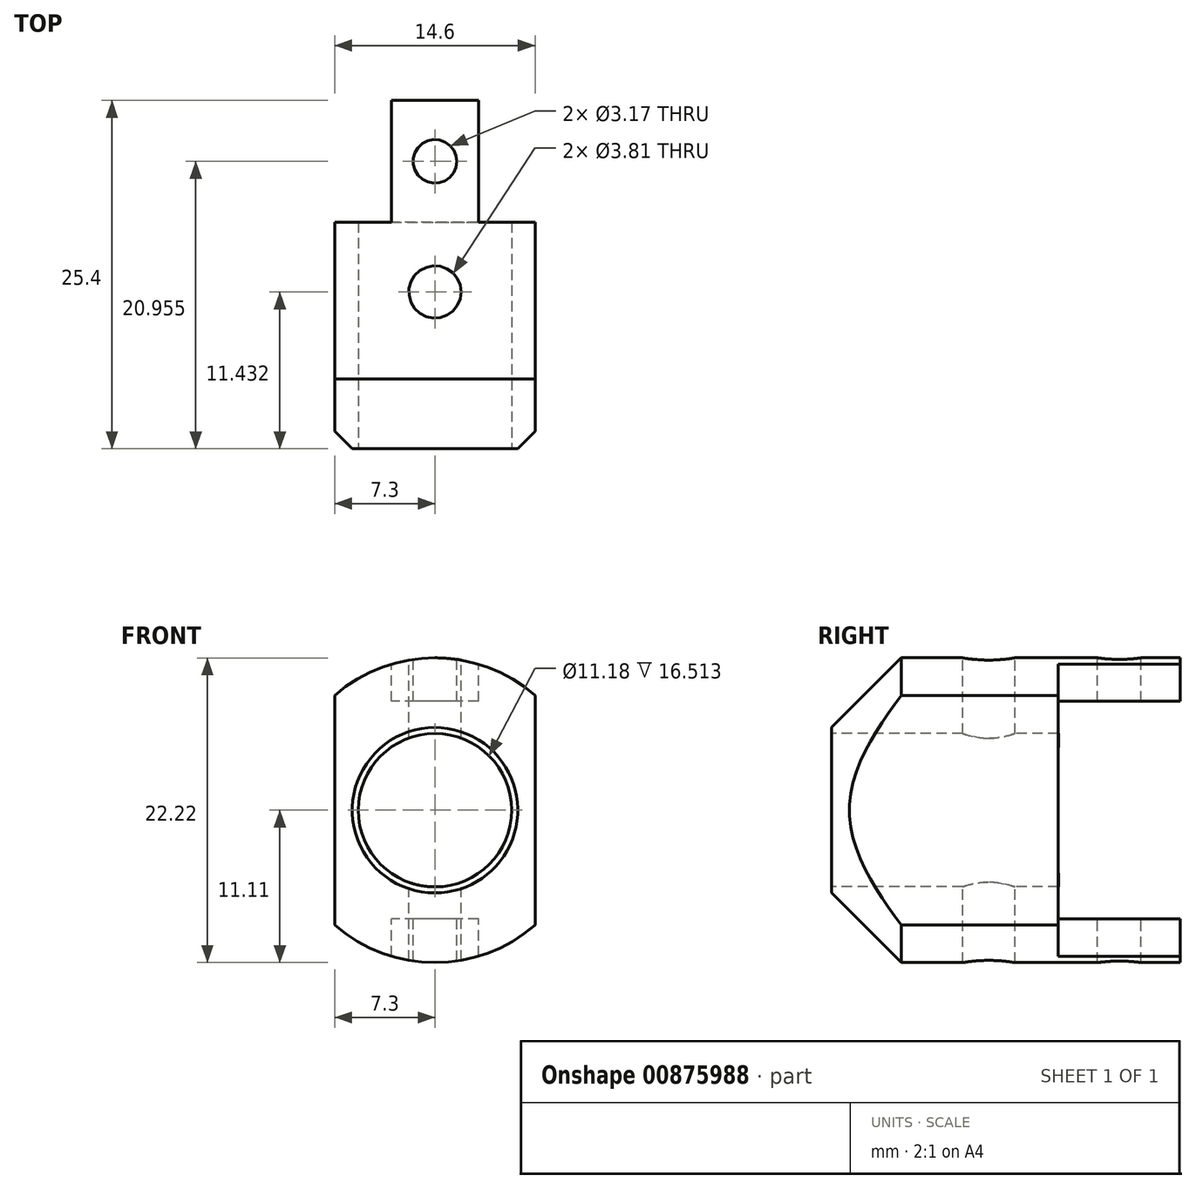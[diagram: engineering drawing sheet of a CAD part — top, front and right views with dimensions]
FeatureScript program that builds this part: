
annotation { "Feature Type Name" : "Feature", "Feature Type Description" : "" }
export const myFeature = defineFeature(function(context is Context, id is Id, definition is map)
    precondition{}
    {
        {
            var Q0;
            Q0=qCreatedBy(makeId("Front.planeOp"),FACE);
            var sketch = newSketch(context, id + "F0", { "sketchPlane" : qUnion([Q0])});
            skCircle(sketch, "E0", {"center": v(0, 0) * mm, "radius": 11.11 * mm});
            skSolve(sketch);
        }
        {
            var Q0;
            Q0=makeQuery(id+"F0.imprint","IMPRINT",FACE,{"disambiguationData":[TD([[makeQuery(id+"F0.imprint","IMPRINT",EDGE,{"derivedFrom":sQuery(id+"F0.wireOp",EDGE,"E0")}),1.0]])]});
            extrude(context, id + "F1", {"entities" : qUnion([Q0]), "endBound" : BoundingType.SYMMETRIC, "depth" : 25.4 * mm, "offsetDistance" : 25.4 * mm});
        }
        {
            var Q0;
            Q0=makeQuery(id+"F1.opExtrude","CAP_FACE",FACE,{"disambiguationData":[OSD([sQuery(id+"F0.wireOp",EDGE,"E0")])],"isStart":false});
            var sketch = newSketch(context, id + "F2", { "sketchPlane" : qUnion([Q0])});
            skCircle(sketch, "E1", {"center": v(0, 0) * mm, "radius": 5.59 * mm});
            skSolve(sketch);
        }
        {
            var Q0;
            Q0=makeQuery(id+"F2.imprint","IMPRINT",FACE,{"disambiguationData":[TD([[makeQuery(id+"F2.imprint","IMPRINT",EDGE,{"derivedFrom":sQuery(id+"F2.wireOp",EDGE,"E1")}),1.0]])]});
            extrude(context, id + "F3", {"entities" : qUnion([Q0]), "operationType" : NewBodyOperationType.REMOVE, "oppositeDirection" : true, "depth" : 31.75 * mm, "offsetDistance" : 25.4 * mm});
        }
        {
            var Q0;
            Q0=makeQuery(id+"F1.opExtrude","CAP_EDGE",EDGE,{"disambiguationData":[OSD([sQuery(id+"F0.wireOp",EDGE,"E0")])],"isStart":false});
            chamfer(context, id + "F4", {"entities" : qUnion([Q0]), "width" : 5.08 * mm, "tangentPropagation" : true});
        }
        {
            var Q0;
            Q0=makeQuery(id+"F1.opExtrude","CAP_FACE",FACE,{"disambiguationData":[OSD([sQuery(id+"F0.wireOp",EDGE,"E0")])],"isStart":true});
            var sketch = newSketch(context, id + "F5", { "sketchPlane" : qUnion([Q0])});
            skLineSegment(sketch, "E2.0", {"start": v(-7.3, 8.38) * mm, "end": v(-7.3, -8.38) * mm});
            skLineSegment(sketch, "E3.MirrorCS", {"start": v(7.3, 8.38) * mm, "end": v(7.3, -8.38) * mm});
            skArc(sketch, "E4", {"start": v(-7.3, 8.38) * mm, "mid": v(-11.11, 0) * mm, "end": v(-7.3, -8.38) * mm});
            skPoint(sketch, "E5.orphan", {"position": v(7.3, 14.3) * mm});
            skPoint(sketch, "E6.orphan", {"position": v(7.3, -21.1) * mm});
            skArc(sketch, "E7.trimOffspring", {"start": v(7.3, -8.38) * mm, "mid": v(11.11, 0) * mm, "end": v(7.3, 8.38) * mm});
            skPoint(sketch, "E8.orphan", {"position": v(-7.3, -21.1) * mm});
            skPoint(sketch, "E9.orphan", {"position": v(-7.3, 14.3) * mm});
            skPoint(sketch, "E10.orphan", {"position": v(0, 14.3) * mm});
            skSolve(sketch);
        }
        {
            var Q0;
            Q0=makeQuery(id+"F5.imprint","IMPRINT",FACE,{"disambiguationData":[TD([[makeQuery(id+"F5.imprint","IMPRINT",EDGE,{"derivedFrom":sQuery(id+"F5.wireOp",EDGE,"E3.MirrorCS")}),1.0]])]});
            var Q1;
            Q1=makeQuery(id+"F5.imprint","IMPRINT",FACE,{"disambiguationData":[TD([[makeQuery(id+"F5.imprint","IMPRINT",EDGE,{"derivedFrom":sQuery(id+"F5.wireOp",EDGE,"E2.0")}),-1.0]])]});
            extrude(context, id + "F6", {"entities" : qUnion([Q0, Q1]), "operationType" : NewBodyOperationType.REMOVE, "oppositeDirection" : true, "depth" : 31.75 * mm, "offsetDistance" : 25.4 * mm});
        }
        {
            var Q0;
            Q0=qCreatedBy(makeId("Top.planeOp"),FACE);
            cPlane(context, id + "F7", {"entities" : qUnion([Q0]), "cplaneType" : CPlaneType.OFFSET, "offset" : 11.1 * mm, "width" : 152.4 * mm, "height" : 152.4 * mm});
        }
        {
            var Q0;
            Q0=qCreatedBy(id+"F7.planeOp",FACE);
            var sketch = newSketch(context, id + "F8", { "sketchPlane" : qUnion([Q0])});
            skLineSegment(sketch, "E11", {"start": v(0, -12.7) * mm, "end": v(0, -1.27) * mm});
            skCircle(sketch, "E12", {"center": v(0, -1.27) * mm, "radius": 1.9 * mm});
            skLineSegment(sketch, "E13", {"start": v(0, 12.7) * mm, "end": v(0, 3.81) * mm});
            skLineSegment(sketch, "E14.0", {"start": v(-3.18, 12.7) * mm, "end": v(-3.18, 3.81) * mm});
            skLineSegment(sketch, "E15", {"start": v(-3.18, 3.81) * mm, "end": v(-7.3, 3.81) * mm});
            skLineSegment(sketch, "E16", {"start": v(-3.18, 12.7) * mm, "end": v(-7.3, 12.7) * mm});
            skLineSegment(sketch, "E17.0", {"start": v(-7.3, 12.7) * mm, "end": v(-7.3, 3.81) * mm});
            skLineSegment(sketch, "E18.MirrorCS", {"start": v(3.18, 12.7) * mm, "end": v(3.18, 3.81) * mm});
            skLineSegment(sketch, "E19.MirrorCS", {"start": v(3.18, 12.7) * mm, "end": v(7.3, 12.7) * mm});
            skLineSegment(sketch, "E20.MirrorCS", {"start": v(7.3, 12.7) * mm, "end": v(7.3, 3.81) * mm});
            skLineSegment(sketch, "E21.MirrorCS", {"start": v(3.18, 3.81) * mm, "end": v(7.3, 3.81) * mm});
            skCircle(sketch, "E22", {"center": v(0, 8.26) * mm, "radius": 1.59 * mm});
            skSolve(sketch);
        }
        {
            var Q0;
            Q0=makeQuery(id+"F8.imprint","IMPRINT",FACE,{"disambiguationData":[TD([[makeQuery(id+"F8.imprint","IMPRINT",EDGE,{"derivedFrom":sQuery(id+"F8.wireOp",EDGE,"E14.0")}),-1.0]])]});
            var Q1;
            Q1=makeQuery(id+"F8.imprint","IMPRINT",FACE,{"disambiguationData":[TD([[makeQuery(id+"F8.imprint","IMPRINT",EDGE,{"derivedFrom":sQuery(id+"F8.wireOp",EDGE,"E18.MirrorCS")}),1.0]])]});
            var Q2;
            Q2=makeQuery(id+"F8.imprint","IMPRINT",FACE,{"disambiguationData":[TD([[makeQuery(id+"F8.imprint","IMPRINT",EDGE,{"derivedFrom":sQuery(id+"F8.wireOp",EDGE,"E12")}),1.0]])]});
            extrude(context, id + "F9", {"entities" : qUnion([Q0, Q1, Q2]), "operationType" : NewBodyOperationType.REMOVE, "oppositeDirection" : true, "depth" : 25.4 * mm, "offsetDistance" : 25.4 * mm});
        }
        {
            var Q0;
            {var subQ0=sQuery(id+"F8.wireOp",EDGE,"E22");var subQ1=sQuery(id+"F8.wireOp",EDGE,"E13");var subQ2=makeQuery(id+"F8.imprint","INTERSECT",VERTEX,{"disambiguationData":[OD(0.0)],"derivedFrom":[subQ1,subQ0]});Q0=makeQuery(id+"F8.imprint","IMPRINT",FACE,{"disambiguationData":[TD([[makeQuery(id+"F8.imprint","IMPRINT",EDGE,{"disambiguationData":[TD([[subQ2,1.0]])],"derivedFrom":subQ1}),-1.0]])]});}
            var Q1;
            {var subQ0=sQuery(id+"F8.wireOp",EDGE,"E22");var subQ1=sQuery(id+"F8.wireOp",EDGE,"E13");var subQ2=makeQuery(id+"F8.imprint","INTERSECT",VERTEX,{"disambiguationData":[OD(0.0)],"derivedFrom":[subQ1,subQ0]});Q1=makeQuery(id+"F8.imprint","IMPRINT",FACE,{"disambiguationData":[TD([[makeQuery(id+"F8.imprint","IMPRINT",EDGE,{"disambiguationData":[TD([[subQ2,1.0]])],"derivedFrom":subQ1}),1.0]])]});}
            extrude(context, id + "F10", {"entities" : qUnion([Q0, Q1]), "operationType" : NewBodyOperationType.REMOVE, "oppositeDirection" : true, "depth" : 25.4 * mm, "offsetDistance" : 25.4 * mm});
        }
        {
            var Q0;
            Q0=qCreatedBy(makeId("Right.planeOp"),FACE);
            cPlane(context, id + "F11", {"entities" : qUnion([Q0]), "cplaneType" : CPlaneType.OFFSET, "offset" : 25.4 * mm, "width" : 152.4 * mm, "height" : 152.4 * mm});
        }
        {
            var Q0;
            Q0=qCreatedBy(id+"F11.planeOp",FACE);
            var sketch = newSketch(context, id + "F12", { "sketchPlane" : qUnion([Q0])});
            skLineSegment(sketch, "E23", {"start": v(7.83, 0) * mm, "end": v(0, 0) * mm});
            skLineSegment(sketch, "E24.0", {"start": v(13.47, 7.94) * mm, "end": v(3.81, 7.94) * mm});
            skLineSegment(sketch, "E25", {"start": v(3.81, 7.94) * mm, "end": v(3.81, 0) * mm});
            skLineSegment(sketch, "E26", {"start": v(3.81, 0) * mm, "end": v(13.47, 0) * mm});
            skLineSegment(sketch, "E27", {"start": v(13.47, 0) * mm, "end": v(13.47, 7.94) * mm});
            skLineSegment(sketch, "E28.MirrorCS", {"start": v(13.47, 0) * mm, "end": v(13.47, -7.94) * mm});
            skLineSegment(sketch, "E29.MirrorCS", {"start": v(13.47, -7.94) * mm, "end": v(3.81, -7.94) * mm});
            skLineSegment(sketch, "E30.MirrorCS", {"start": v(3.81, -7.94) * mm, "end": v(3.81, 0) * mm});
            skSolve(sketch);
        }
        {
            var Q0;
            Q0=makeQuery(id+"F12.imprint","IMPRINT",FACE,{"disambiguationData":[TD([[makeQuery(id+"F12.imprint","IMPRINT",EDGE,{"derivedFrom":sQuery(id+"F12.wireOp",EDGE,"E24.0")}),1.0]])]});
            var Q1;
            {var subQ0=sQuery(id+"F12.wireOp",EDGE,"E28.MirrorCS");Q1=makeQuery(id+"F12.imprint","IMPRINT",FACE,{"disambiguationData":[TD([[makeQuery(id+"F12.imprint","IMPRINT",EDGE,{"derivedFrom":subQ0}),-1.0]])]});}
            extrude(context, id + "F13", {"entities" : qUnion([Q0, Q1]), "operationType" : NewBodyOperationType.REMOVE, "oppositeDirection" : true, "depth" : 50.8 * mm, "offsetDistance" : 25.4 * mm});
        }
    });
